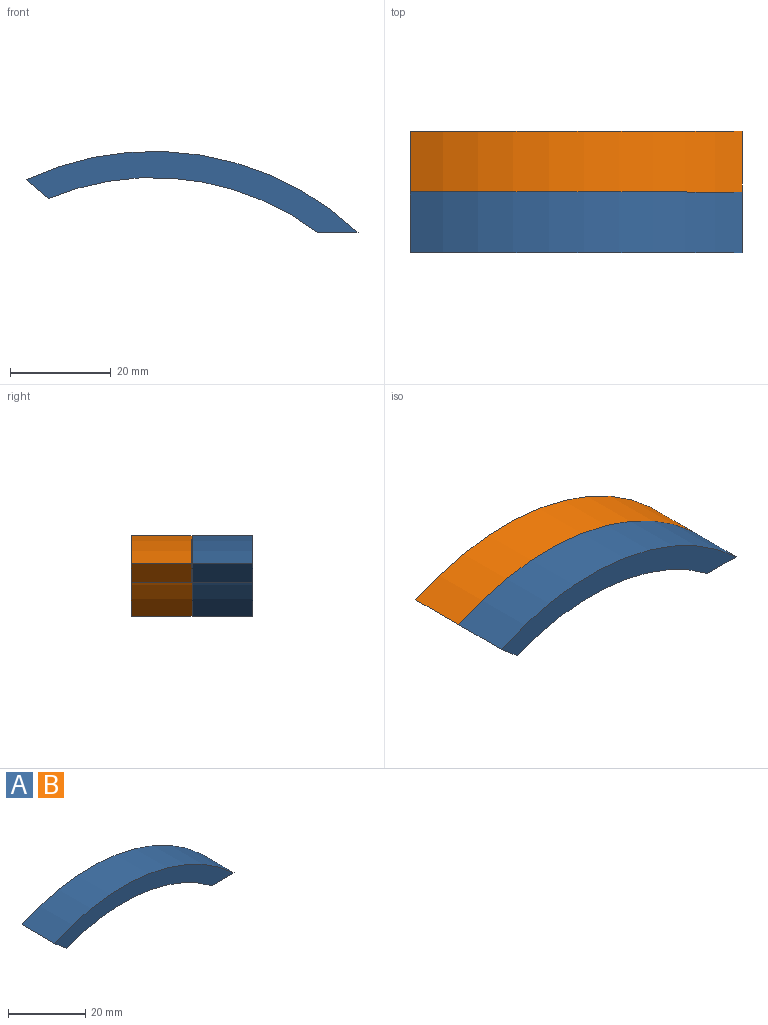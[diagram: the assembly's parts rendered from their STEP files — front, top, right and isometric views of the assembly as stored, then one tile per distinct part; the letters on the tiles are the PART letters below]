
ASSEMBLY  parts=2 mates=1
PART A: 6 faces, bbox 65.8x12x16.1 mm
  f0: cylinder r=54.02mm len=53.31mm, axis (0,1,0), area 674.9mm2, adj f1,f3,f4,f5
  f1: plane 12x8.05mm, normal (0,0,-1), area 96.6mm2, adj f0,f2,f4,f5
  f2: cylinder r=59.21mm len=65.76mm, axis (0,1,0), area 848.5mm2, adj f1,f3,f4,f5
  f3: plane 12x4.4mm, normal (-0.65,0,-0.76), area 69.2mm2, adj f0,f2,f4,f5
  f4: plane 65.76x16.06mm, normal (0,-1,0), area 330mm2, adj f0,f1,f2,f3
  f5: plane 65.76x16.06mm, normal (0,1,0), area 330mm2, adj f0,f1,f2,f3
PART B: same geometry as A
PLACE A t=(-12.88,13.37,-20.61)mm
PLACE B t=(-12.88,25.37,-20.61)mm
MATE fastened B.f4 <-> A.f5  axis (0,-1,0) through (52.12,13.37,-20.61)mm
